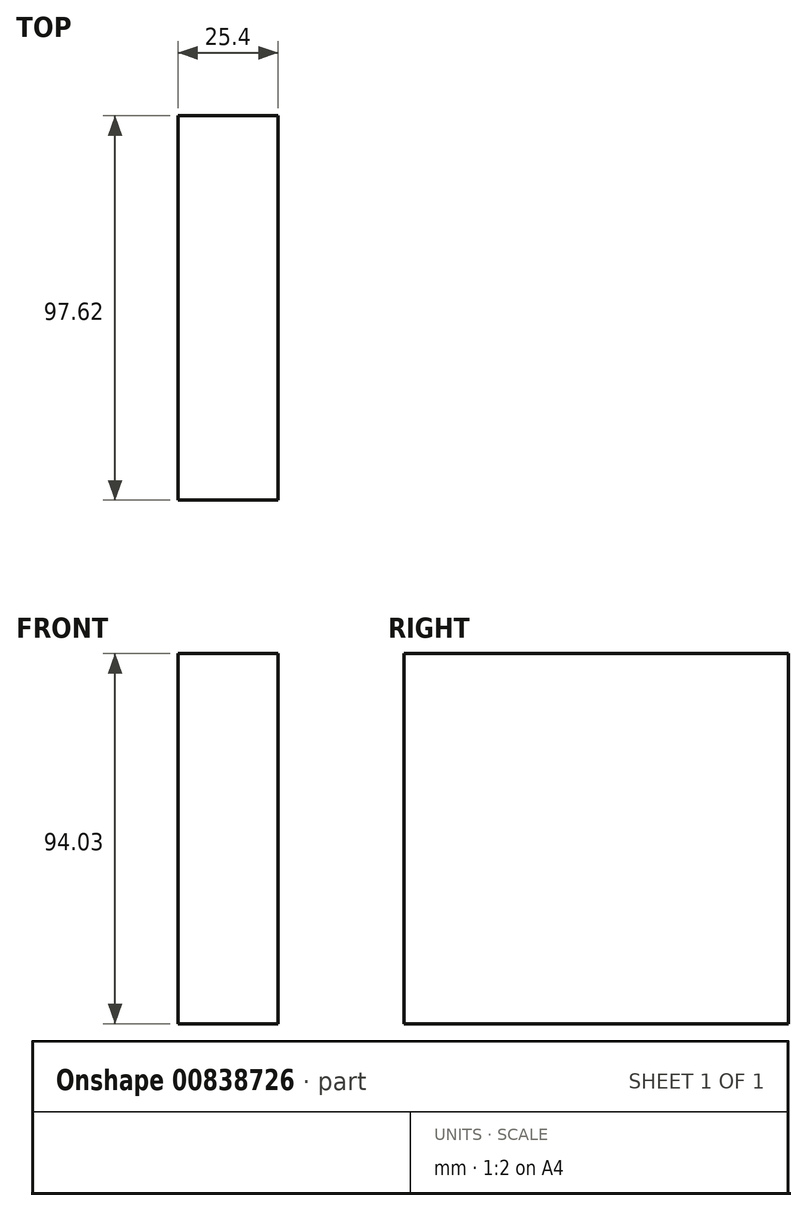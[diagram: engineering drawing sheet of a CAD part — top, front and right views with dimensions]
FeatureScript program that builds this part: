
annotation { "Feature Type Name" : "Feature", "Feature Type Description" : "" }
export const myFeature = defineFeature(function(context is Context, id is Id, definition is map)
    precondition{}
    {
        {
            var Q0;
            Q0=qCreatedBy(makeId("Right.planeOp"),FACE);
            var sketch = newSketch(context, id + "F0", { "sketchPlane" : qUnion([Q0])});
            skLineSegment(sketch, "E0.bottom", {"start": v(46.45, 47.82) * mm, "end": v(-51.17, 47.82) * mm});
            skLineSegment(sketch, "E0.top", {"start": v(46.45, -46.2) * mm, "end": v(-51.17, -46.2) * mm});
            skLineSegment(sketch, "E0.left", {"start": v(46.45, 47.82) * mm, "end": v(46.45, -46.2) * mm});
            skLineSegment(sketch, "E0.right", {"start": v(-51.17, 47.82) * mm, "end": v(-51.17, -46.2) * mm});
            skSolve(sketch);
        }
        {
            var Q0;
            Q0 = qSketchRegion(id + "F0", true);
            extrude(context, id + "F1", {"entities" : qUnion([Q0]), "depth" : 25.4 * mm, "offsetDistance" : 25.4 * mm});
        }
    });
